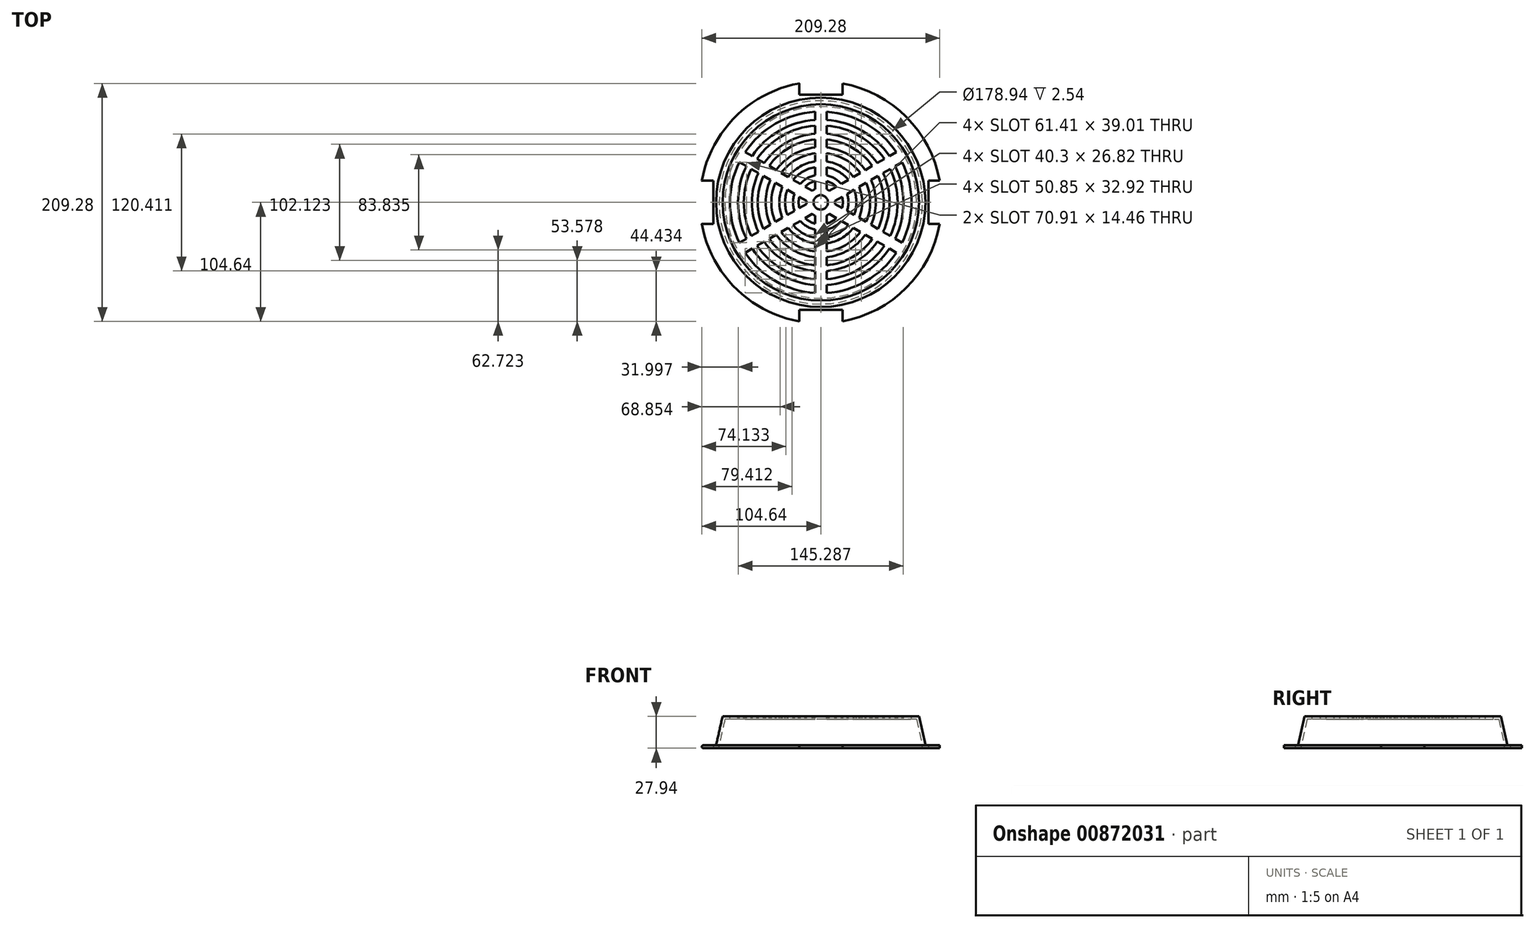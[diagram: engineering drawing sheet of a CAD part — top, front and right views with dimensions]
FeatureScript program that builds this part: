
annotation { "Feature Type Name" : "Feature", "Feature Type Description" : "" }
export const myFeature = defineFeature(function(context is Context, id is Id, definition is map)
    precondition{}
    {
        {
            var Q0;
            Q0=qCreatedBy(makeId("Front.planeOp"),FACE);
            var sketch = newSketch(context, id + "F0", { "sketchPlane" : qUnion([Q0])});
            skLineSegment(sketch, "E0", {"start": v(0, 0) * mm, "end": v(0, 69.45) * mm, "construction": true});
            skLineSegment(sketch, "E1", {"start": v(0, 0) * mm, "end": v(-92.08, 0) * mm});
            skLineSegment(sketch, "E2", {"start": v(-92.08, 0) * mm, "end": v(-86.36, 25.4) * mm});
            skLineSegment(sketch, "E3", {"start": v(-86.36, 25.4) * mm, "end": v(0, 25.4) * mm});
            skLineSegment(sketch, "E4", {"start": v(0, 25.4) * mm, "end": v(0, 0) * mm});
            skSolve(sketch);
        }
        {
            var Q0;
            Q0=makeQuery(id+"F0.imprint","IMPRINT",FACE,{"disambiguationData":[TD([[makeQuery(id+"F0.imprint","IMPRINT",EDGE,{"derivedFrom":sQuery(id+"F0.wireOp",EDGE,"E1")}),-1.0]])]});
            var Q1;
            Q1=sQuery(id+"F0.wireOp",EDGE,"E0");
            revolve(context, id + "F1", {"surfaceOperationType" : NewSurfaceOperationType.NEW, "entities" : qUnion([Q0]), "axis" : qUnion([Q1]), "revolveType" : RevolveType.FULL});
        }
        {
            var Q0;
            Q0=makeQuery(id+"F1.opRevolve","SWEPT_FACE",FACE,{"disambiguationData":[OSD([sQuery(id+"F0.wireOp",EDGE,"E1")])]});
            shell(context, id + "F2", {"entities" : qUnion([Q0]), "thickness" : 2.54 * mm});
        }
        {
            var Q0;
            Q0=makeQuery(id+"F1.opRevolve","SWEPT_FACE",FACE,{"disambiguationData":[OSD([sQuery(id+"F0.wireOp",EDGE,"E1")])]});
            var sketch = newSketch(context, id + "F3", { "sketchPlane" : qUnion([Q0])});
            skCircle(sketch, "E5.0", {"center": v(0, 0) * mm, "radius": 89.47 * mm});
            skCircle(sketch, "E6", {"center": v(0, 0) * mm, "radius": 106.36 * mm});
            skSolve(sketch);
        }
        {
            var Q0;
            Q0 = qSketchRegion(id + "F3", true);
            extrude(context, id + "F4", {"entities" : qUnion([Q0]), "operationType" : NewBodyOperationType.ADD, "depth" : 2.54 * mm, "offsetDistance" : 25.4 * mm});
        }
        {
            var Q0;
            Q0=makeQuery(id+"F1.opRevolve","SWEPT_FACE",FACE,{"disambiguationData":[OSD([sQuery(id+"F0.wireOp",EDGE,"E3")])]});
            var sketch = newSketch(context, id + "F5", { "sketchPlane" : qUnion([Q0])});
            skLineSegment(sketch, "E7", {"start": v(0, 0) * mm, "end": v(0, 86.36) * mm, "construction": true});
            skLineSegment(sketch, "E8", {"start": v(0, 0) * mm, "end": v(74.79, 43.18) * mm, "construction": true});
            skArc(sketch, "E9", {"start": v(5.08, 23.83) * mm, "mid": v(12.18, 21.1) * mm, "end": v(18.1, 16.32) * mm});
            skArc(sketch, "E10", {"start": v(5.08, 18.75) * mm, "mid": v(9.71, 16.82) * mm, "end": v(13.7, 13.78) * mm});
            skArc(sketch, "E11", {"start": v(5.08, 30.94) * mm, "mid": v(15.68, 27.16) * mm, "end": v(24.26, 19.87) * mm});
            skArc(sketch, "E12", {"start": v(5.08, 11.64) * mm, "mid": v(6.35, 11) * mm, "end": v(7.54, 10.22) * mm});
            skLineSegment(sketch, "E13", {"start": v(24.26, 19.87) * mm, "end": v(18.1, 16.32) * mm});
            skLineSegment(sketch, "E14", {"start": v(5.08, 23.83) * mm, "end": v(5.08, 30.94) * mm});
            skLineSegment(sketch, "E15", {"start": v(5.08, 18.75) * mm, "end": v(5.08, 11.64) * mm});
            skLineSegment(sketch, "E16", {"start": v(7.54, 10.22) * mm, "end": v(13.7, 13.78) * mm});
            skArc(sketch, "E17", {"start": v(5.08, 36.02) * mm, "mid": v(18.2, 31.5) * mm, "end": v(28.66, 22.41) * mm});
            skArc(sketch, "E18", {"start": v(5.08, 43.14) * mm, "mid": v(21.72, 37.61) * mm, "end": v(34.82, 25.97) * mm});
            skLineSegment(sketch, "E19", {"start": v(5.08, 36.02) * mm, "end": v(5.08, 43.14) * mm});
            skLineSegment(sketch, "E20", {"start": v(28.66, 22.41) * mm, "end": v(34.82, 25.97) * mm});
            skArc(sketch, "E21", {"start": v(5.08, 48.22) * mm, "mid": v(24.24, 41.99) * mm, "end": v(39.22, 28.5) * mm});
            skArc(sketch, "E22", {"start": v(5.08, 55.33) * mm, "mid": v(27.78, 48.12) * mm, "end": v(45.38, 32.06) * mm});
            skLineSegment(sketch, "E23", {"start": v(5.08, 48.22) * mm, "end": v(5.08, 55.33) * mm});
            skLineSegment(sketch, "E24", {"start": v(39.22, 28.5) * mm, "end": v(45.38, 32.06) * mm});
            skArc(sketch, "E25.1.0", {"start": v(-45.38, 32.06) * mm, "mid": v(-27.78, 48.12) * mm, "end": v(-5.08, 55.33) * mm});
            skLineSegment(sketch, "E25.1.1", {"start": v(-5.08, 48.22) * mm, "end": v(-5.08, 55.33) * mm});
            skArc(sketch, "E25.1.2", {"start": v(-39.22, 28.5) * mm, "mid": v(-24.24, 41.99) * mm, "end": v(-5.08, 48.22) * mm});
            skLineSegment(sketch, "E25.1.3", {"start": v(-39.22, 28.5) * mm, "end": v(-45.38, 32.06) * mm});
            skLineSegment(sketch, "E25.1.4", {"start": v(-28.66, 22.41) * mm, "end": v(-34.82, 25.97) * mm});
            skArc(sketch, "E25.1.5", {"start": v(-34.82, 25.97) * mm, "mid": v(-21.72, 37.61) * mm, "end": v(-5.08, 43.14) * mm});
            skLineSegment(sketch, "E25.1.6", {"start": v(-5.08, 36.02) * mm, "end": v(-5.08, 43.14) * mm});
            skArc(sketch, "E25.1.7", {"start": v(-28.66, 22.41) * mm, "mid": v(-18.2, 31.5) * mm, "end": v(-5.08, 36.02) * mm});
            skArc(sketch, "E25.1.8", {"start": v(-24.26, 19.87) * mm, "mid": v(-15.68, 27.16) * mm, "end": v(-5.08, 30.94) * mm});
            skLineSegment(sketch, "E25.1.9", {"start": v(-18.1, 16.32) * mm, "end": v(-24.26, 19.87) * mm});
            skArc(sketch, "E25.1.10", {"start": v(-18.1, 16.32) * mm, "mid": v(-12.18, 21.1) * mm, "end": v(-5.08, 23.83) * mm});
            skLineSegment(sketch, "E25.1.11", {"start": v(-5.08, 30.94) * mm, "end": v(-5.08, 23.83) * mm});
            skArc(sketch, "E25.1.12", {"start": v(-13.7, 13.78) * mm, "mid": v(-9.71, 16.82) * mm, "end": v(-5.08, 18.75) * mm});
            skLineSegment(sketch, "E25.1.13", {"start": v(-13.7, 13.78) * mm, "end": v(-7.54, 10.22) * mm});
            skArc(sketch, "E25.1.14", {"start": v(-7.54, 10.22) * mm, "mid": v(-6.35, 11) * mm, "end": v(-5.08, 11.64) * mm});
            skLineSegment(sketch, "E25.1.15", {"start": v(-5.08, 11.64) * mm, "end": v(-5.08, 18.75) * mm});
            skArc(sketch, "E25.2.0", {"start": v(-50.46, -23.26) * mm, "mid": v(-55.56, 0) * mm, "end": v(-50.46, 23.26) * mm});
            skLineSegment(sketch, "E25.2.1", {"start": v(-44.3, 19.7) * mm, "end": v(-50.46, 23.26) * mm});
            skArc(sketch, "E25.2.2", {"start": v(-44.3, -19.7) * mm, "mid": v(-48.48, 0) * mm, "end": v(-44.3, 19.7) * mm});
            skLineSegment(sketch, "E25.2.3", {"start": v(-44.3, -19.7) * mm, "end": v(-50.46, -23.26) * mm});
            skLineSegment(sketch, "E25.2.4", {"start": v(-33.74, -13.61) * mm, "end": v(-39.9, -17.17) * mm});
            skArc(sketch, "E25.2.5", {"start": v(-39.9, -17.17) * mm, "mid": v(-43.43, 0) * mm, "end": v(-39.9, 17.17) * mm});
            skLineSegment(sketch, "E25.2.6", {"start": v(-33.74, 13.61) * mm, "end": v(-39.9, 17.17) * mm});
            skArc(sketch, "E25.2.7", {"start": v(-33.74, -13.61) * mm, "mid": v(-36.38, 0) * mm, "end": v(-33.74, 13.61) * mm});
            skArc(sketch, "E25.2.8", {"start": v(-29.34, -11.07) * mm, "mid": v(-31.36, 0) * mm, "end": v(-29.34, 11.07) * mm});
            skLineSegment(sketch, "E25.2.9", {"start": v(-23.18, -7.52) * mm, "end": v(-29.34, -11.07) * mm});
            skArc(sketch, "E25.2.10", {"start": v(-23.18, -7.52) * mm, "mid": v(-24.37, 0) * mm, "end": v(-23.18, 7.52) * mm});
            skLineSegment(sketch, "E25.2.11", {"start": v(-29.34, 11.07) * mm, "end": v(-23.18, 7.52) * mm});
            skArc(sketch, "E25.2.12", {"start": v(-18.78, -4.98) * mm, "mid": v(-19.43, 0) * mm, "end": v(-18.78, 4.98) * mm});
            skLineSegment(sketch, "E25.2.13", {"start": v(-18.78, -4.98) * mm, "end": v(-12.62, -1.42) * mm});
            skArc(sketch, "E25.2.14", {"start": v(-12.62, -1.42) * mm, "mid": v(-12.7, 0) * mm, "end": v(-12.62, 1.42) * mm});
            skLineSegment(sketch, "E25.2.15", {"start": v(-12.62, 1.42) * mm, "end": v(-18.78, 4.98) * mm});
            skArc(sketch, "E25.3.0", {"start": v(-5.08, -55.33) * mm, "mid": v(-27.78, -48.12) * mm, "end": v(-45.38, -32.06) * mm});
            skLineSegment(sketch, "E25.3.1", {"start": v(-39.22, -28.5) * mm, "end": v(-45.38, -32.06) * mm});
            skArc(sketch, "E25.3.2", {"start": v(-5.08, -48.22) * mm, "mid": v(-24.24, -41.99) * mm, "end": v(-39.22, -28.5) * mm});
            skLineSegment(sketch, "E25.3.3", {"start": v(-5.08, -48.22) * mm, "end": v(-5.08, -55.33) * mm});
            skLineSegment(sketch, "E25.3.4", {"start": v(-5.08, -36.02) * mm, "end": v(-5.08, -43.14) * mm});
            skArc(sketch, "E25.3.5", {"start": v(-5.08, -43.14) * mm, "mid": v(-21.72, -37.61) * mm, "end": v(-34.82, -25.97) * mm});
            skLineSegment(sketch, "E25.3.6", {"start": v(-28.66, -22.41) * mm, "end": v(-34.82, -25.97) * mm});
            skArc(sketch, "E25.3.7", {"start": v(-5.08, -36.02) * mm, "mid": v(-18.2, -31.5) * mm, "end": v(-28.66, -22.41) * mm});
            skArc(sketch, "E25.3.8", {"start": v(-5.08, -30.94) * mm, "mid": v(-15.68, -27.16) * mm, "end": v(-24.26, -19.87) * mm});
            skLineSegment(sketch, "E25.3.9", {"start": v(-5.08, -23.83) * mm, "end": v(-5.08, -30.94) * mm});
            skArc(sketch, "E25.3.10", {"start": v(-5.08, -23.83) * mm, "mid": v(-12.18, -21.1) * mm, "end": v(-18.1, -16.32) * mm});
            skLineSegment(sketch, "E25.3.11", {"start": v(-24.26, -19.87) * mm, "end": v(-18.1, -16.32) * mm});
            skArc(sketch, "E25.3.12", {"start": v(-5.08, -18.75) * mm, "mid": v(-9.71, -16.82) * mm, "end": v(-13.7, -13.78) * mm});
            skLineSegment(sketch, "E25.3.13", {"start": v(-5.08, -18.75) * mm, "end": v(-5.08, -11.64) * mm});
            skArc(sketch, "E25.3.14", {"start": v(-5.08, -11.64) * mm, "mid": v(-6.35, -11) * mm, "end": v(-7.54, -10.22) * mm});
            skLineSegment(sketch, "E25.3.15", {"start": v(-7.54, -10.22) * mm, "end": v(-13.7, -13.78) * mm});
            skArc(sketch, "E25.4.0", {"start": v(45.38, -32.06) * mm, "mid": v(27.78, -48.12) * mm, "end": v(5.08, -55.33) * mm});
            skLineSegment(sketch, "E25.4.1", {"start": v(5.08, -48.22) * mm, "end": v(5.08, -55.33) * mm});
            skArc(sketch, "E25.4.2", {"start": v(39.22, -28.5) * mm, "mid": v(24.24, -41.99) * mm, "end": v(5.08, -48.22) * mm});
            skLineSegment(sketch, "E25.4.3", {"start": v(39.22, -28.5) * mm, "end": v(45.38, -32.06) * mm});
            skLineSegment(sketch, "E25.4.4", {"start": v(28.66, -22.41) * mm, "end": v(34.82, -25.97) * mm});
            skArc(sketch, "E25.4.5", {"start": v(34.82, -25.97) * mm, "mid": v(21.72, -37.61) * mm, "end": v(5.08, -43.14) * mm});
            skLineSegment(sketch, "E25.4.6", {"start": v(5.08, -36.02) * mm, "end": v(5.08, -43.14) * mm});
            skArc(sketch, "E25.4.7", {"start": v(28.66, -22.41) * mm, "mid": v(18.2, -31.5) * mm, "end": v(5.08, -36.02) * mm});
            skArc(sketch, "E25.4.8", {"start": v(24.26, -19.87) * mm, "mid": v(15.68, -27.16) * mm, "end": v(5.08, -30.94) * mm});
            skLineSegment(sketch, "E25.4.9", {"start": v(18.1, -16.32) * mm, "end": v(24.26, -19.87) * mm});
            skArc(sketch, "E25.4.10", {"start": v(18.1, -16.32) * mm, "mid": v(12.18, -21.1) * mm, "end": v(5.08, -23.83) * mm});
            skLineSegment(sketch, "E25.4.11", {"start": v(5.08, -30.94) * mm, "end": v(5.08, -23.83) * mm});
            skArc(sketch, "E25.4.12", {"start": v(13.7, -13.78) * mm, "mid": v(9.71, -16.82) * mm, "end": v(5.08, -18.75) * mm});
            skLineSegment(sketch, "E25.4.13", {"start": v(13.7, -13.78) * mm, "end": v(7.54, -10.22) * mm});
            skArc(sketch, "E25.4.14", {"start": v(7.54, -10.22) * mm, "mid": v(6.35, -11) * mm, "end": v(5.08, -11.64) * mm});
            skLineSegment(sketch, "E25.4.15", {"start": v(5.08, -11.64) * mm, "end": v(5.08, -18.75) * mm});
            skArc(sketch, "E25.5.0", {"start": v(50.46, 23.26) * mm, "mid": v(55.56, 0) * mm, "end": v(50.46, -23.26) * mm});
            skLineSegment(sketch, "E25.5.1", {"start": v(44.3, -19.7) * mm, "end": v(50.46, -23.26) * mm});
            skArc(sketch, "E25.5.2", {"start": v(44.3, 19.7) * mm, "mid": v(48.48, 0) * mm, "end": v(44.3, -19.7) * mm});
            skLineSegment(sketch, "E25.5.3", {"start": v(44.3, 19.7) * mm, "end": v(50.46, 23.26) * mm});
            skLineSegment(sketch, "E25.5.4", {"start": v(33.74, 13.61) * mm, "end": v(39.9, 17.17) * mm});
            skArc(sketch, "E25.5.5", {"start": v(39.9, 17.17) * mm, "mid": v(43.43, 0) * mm, "end": v(39.9, -17.17) * mm});
            skLineSegment(sketch, "E25.5.6", {"start": v(33.74, -13.61) * mm, "end": v(39.9, -17.17) * mm});
            skArc(sketch, "E25.5.7", {"start": v(33.74, 13.61) * mm, "mid": v(36.38, 0) * mm, "end": v(33.74, -13.61) * mm});
            skArc(sketch, "E25.5.8", {"start": v(29.34, 11.07) * mm, "mid": v(31.36, 0) * mm, "end": v(29.34, -11.07) * mm});
            skLineSegment(sketch, "E25.5.9", {"start": v(23.18, 7.52) * mm, "end": v(29.34, 11.07) * mm});
            skArc(sketch, "E25.5.10", {"start": v(23.18, 7.52) * mm, "mid": v(24.37, 0) * mm, "end": v(23.18, -7.52) * mm});
            skLineSegment(sketch, "E25.5.11", {"start": v(29.34, -11.07) * mm, "end": v(23.18, -7.52) * mm});
            skArc(sketch, "E25.5.12", {"start": v(18.78, 4.98) * mm, "mid": v(19.43, 0) * mm, "end": v(18.78, -4.98) * mm});
            skLineSegment(sketch, "E25.5.13", {"start": v(18.78, 4.98) * mm, "end": v(12.62, 1.42) * mm});
            skArc(sketch, "E25.5.14", {"start": v(12.62, 1.42) * mm, "mid": v(12.7, 0) * mm, "end": v(12.62, -1.42) * mm});
            skLineSegment(sketch, "E25.5.15", {"start": v(12.62, -1.42) * mm, "end": v(18.78, -4.98) * mm});
            skArc(sketch, "E26", {"start": v(5.08, 60.4) * mm, "mid": v(30.31, 52.5) * mm, "end": v(49.77, 34.6) * mm});
            skArc(sketch, "E27", {"start": v(5.08, 67.52) * mm, "mid": v(33.86, 58.64) * mm, "end": v(55.93, 38.16) * mm});
            skPoint(sketch, "E27.startSnap0", {"position": v(5.08, 39.58) * mm});
            skLineSegment(sketch, "E28", {"start": v(5.08, 60.4) * mm, "end": v(5.08, 67.52) * mm});
            skLineSegment(sketch, "E29", {"start": v(49.77, 34.6) * mm, "end": v(55.93, 38.16) * mm});
            skArc(sketch, "E30", {"start": v(5.08, 72.6) * mm, "mid": v(36.39, 63.03) * mm, "end": v(60.33, 40.7) * mm});
            skArc(sketch, "E31", {"start": v(5.08, 79.71) * mm, "mid": v(39.94, 69.17) * mm, "end": v(66.5, 44.26) * mm});
            skLineSegment(sketch, "E32", {"start": v(5.08, 72.6) * mm, "end": v(5.08, 79.71) * mm});
            skLineSegment(sketch, "E33", {"start": v(60.33, 40.7) * mm, "end": v(66.5, 44.26) * mm});
            skArc(sketch, "E34.1.0", {"start": v(-49.77, 34.6) * mm, "mid": v(-30.31, 52.5) * mm, "end": v(-5.08, 60.4) * mm});
            skLineSegment(sketch, "E34.1.1", {"start": v(-49.77, 34.6) * mm, "end": v(-55.93, 38.16) * mm});
            skArc(sketch, "E34.1.2", {"start": v(-55.93, 38.16) * mm, "mid": v(-33.86, 58.64) * mm, "end": v(-5.08, 67.52) * mm});
            skLineSegment(sketch, "E34.1.3", {"start": v(-5.08, 60.4) * mm, "end": v(-5.08, 67.52) * mm});
            skLineSegment(sketch, "E34.1.4", {"start": v(-5.08, 72.6) * mm, "end": v(-5.08, 79.71) * mm});
            skArc(sketch, "E34.1.5", {"start": v(-60.33, 40.7) * mm, "mid": v(-36.39, 63.03) * mm, "end": v(-5.08, 72.6) * mm});
            skLineSegment(sketch, "E34.1.6", {"start": v(-60.33, 40.7) * mm, "end": v(-66.5, 44.26) * mm});
            skArc(sketch, "E34.1.7", {"start": v(-66.5, 44.26) * mm, "mid": v(-39.94, 69.17) * mm, "end": v(-5.08, 79.71) * mm});
            skArc(sketch, "E34.2.0", {"start": v(-54.85, -25.8) * mm, "mid": v(-60.62, 0) * mm, "end": v(-54.85, 25.8) * mm});
            skLineSegment(sketch, "E34.2.1", {"start": v(-54.85, -25.8) * mm, "end": v(-61.01, -29.36) * mm});
            skArc(sketch, "E34.2.2", {"start": v(-61.01, -29.36) * mm, "mid": v(-67.71, 0) * mm, "end": v(-61.01, 29.36) * mm});
            skLineSegment(sketch, "E34.2.3", {"start": v(-54.85, 25.8) * mm, "end": v(-61.01, 29.36) * mm});
            skLineSegment(sketch, "E34.2.4", {"start": v(-65.41, 31.9) * mm, "end": v(-71.57, 35.46) * mm});
            skArc(sketch, "E34.2.5", {"start": v(-65.41, -31.9) * mm, "mid": v(-72.78, 0) * mm, "end": v(-65.41, 31.9) * mm});
            skLineSegment(sketch, "E34.2.6", {"start": v(-65.41, -31.9) * mm, "end": v(-71.57, -35.46) * mm});
            skArc(sketch, "E34.2.7", {"start": v(-71.57, -35.46) * mm, "mid": v(-79.87, 0) * mm, "end": v(-71.57, 35.46) * mm});
            skArc(sketch, "E34.3.0", {"start": v(-5.08, -60.4) * mm, "mid": v(-30.31, -52.5) * mm, "end": v(-49.77, -34.6) * mm});
            skLineSegment(sketch, "E34.3.1", {"start": v(-5.08, -60.4) * mm, "end": v(-5.08, -67.52) * mm});
            skArc(sketch, "E34.3.2", {"start": v(-5.08, -67.52) * mm, "mid": v(-33.86, -58.64) * mm, "end": v(-55.93, -38.16) * mm});
            skLineSegment(sketch, "E34.3.3", {"start": v(-49.77, -34.6) * mm, "end": v(-55.93, -38.16) * mm});
            skLineSegment(sketch, "E34.3.4", {"start": v(-60.33, -40.7) * mm, "end": v(-66.5, -44.26) * mm});
            skArc(sketch, "E34.3.5", {"start": v(-5.08, -72.6) * mm, "mid": v(-36.39, -63.03) * mm, "end": v(-60.33, -40.7) * mm});
            skLineSegment(sketch, "E34.3.6", {"start": v(-5.08, -72.6) * mm, "end": v(-5.08, -79.71) * mm});
            skArc(sketch, "E34.3.7", {"start": v(-5.08, -79.71) * mm, "mid": v(-39.94, -69.17) * mm, "end": v(-66.5, -44.26) * mm});
            skArc(sketch, "E34.4.0", {"start": v(49.77, -34.6) * mm, "mid": v(30.31, -52.5) * mm, "end": v(5.08, -60.4) * mm});
            skLineSegment(sketch, "E34.4.1", {"start": v(49.77, -34.6) * mm, "end": v(55.93, -38.16) * mm});
            skArc(sketch, "E34.4.2", {"start": v(55.93, -38.16) * mm, "mid": v(33.86, -58.64) * mm, "end": v(5.08, -67.52) * mm});
            skLineSegment(sketch, "E34.4.3", {"start": v(5.08, -60.4) * mm, "end": v(5.08, -67.52) * mm});
            skLineSegment(sketch, "E34.4.4", {"start": v(5.08, -72.6) * mm, "end": v(5.08, -79.71) * mm});
            skArc(sketch, "E34.4.5", {"start": v(60.33, -40.7) * mm, "mid": v(36.39, -63.03) * mm, "end": v(5.08, -72.6) * mm});
            skLineSegment(sketch, "E34.4.6", {"start": v(60.33, -40.7) * mm, "end": v(66.5, -44.26) * mm});
            skArc(sketch, "E34.4.7", {"start": v(66.5, -44.26) * mm, "mid": v(39.94, -69.17) * mm, "end": v(5.08, -79.71) * mm});
            skArc(sketch, "E34.5.0", {"start": v(54.85, 25.8) * mm, "mid": v(60.62, 0) * mm, "end": v(54.85, -25.8) * mm});
            skLineSegment(sketch, "E34.5.1", {"start": v(54.85, 25.8) * mm, "end": v(61.01, 29.36) * mm});
            skArc(sketch, "E34.5.2", {"start": v(61.01, 29.36) * mm, "mid": v(67.71, 0) * mm, "end": v(61.01, -29.36) * mm});
            skLineSegment(sketch, "E34.5.3", {"start": v(54.85, -25.8) * mm, "end": v(61.01, -29.36) * mm});
            skLineSegment(sketch, "E34.5.4", {"start": v(65.41, -31.9) * mm, "end": v(71.57, -35.46) * mm});
            skArc(sketch, "E34.5.5", {"start": v(65.41, 31.9) * mm, "mid": v(72.78, 0) * mm, "end": v(65.41, -31.9) * mm});
            skLineSegment(sketch, "E34.5.6", {"start": v(65.41, 31.9) * mm, "end": v(71.57, 35.46) * mm});
            skArc(sketch, "E34.5.7", {"start": v(71.57, 35.46) * mm, "mid": v(79.87, 0) * mm, "end": v(71.57, -35.46) * mm});
            skSolve(sketch);
        }
        {
            var Q0;
            Q0 = qSketchRegion(id + "F5", true);
            extrude(context, id + "F6", {"entities" : qUnion([Q0]), "operationType" : NewBodyOperationType.REMOVE, "endBound" : BoundingType.THROUGH_ALL, "oppositeDirection" : true, "depth" : 25.4 * mm, "offsetDistance" : 25.4 * mm});
        }
        {
            var Q0;
            Q0=makeQuery(id+"F4.opExtrude","CAP_FACE",FACE,{"disambiguationData":[OSD([sQuery(id+"F3.wireOp",EDGE,"E5.0"),sQuery(id+"F3.wireOp",EDGE,"E6")])],"isStart":false});
            var sketch = newSketch(context, id + "F7", { "sketchPlane" : qUnion([Q0])});
            skLineSegment(sketch, "E35", {"start": v(-28.47, 0) * mm, "end": v(28.47, 0) * mm, "construction": true});
            skLineSegment(sketch, "E36.bottom", {"start": v(-119.87, 19.05) * mm, "end": v(-94.62, 19.05) * mm});
            skLineSegment(sketch, "E36.top", {"start": v(-119.87, -19.05) * mm, "end": v(-94.62, -19.05) * mm});
            skLineSegment(sketch, "E36.left", {"start": v(-119.87, 19.05) * mm, "end": v(-119.87, -19.05) * mm});
            skLineSegment(sketch, "E36.right", {"start": v(-94.62, 19.05) * mm, "end": v(-94.62, -19.05) * mm});
            skLineSegment(sketch, "E37", {"start": v(-94.61, 19.05) * mm, "end": v(-119.87, -19.05) * mm, "construction": true});
            skPoint(sketch, "E38", {"position": v(-107.24, 0) * mm});
            skLineSegment(sketch, "E39", {"start": v(0, 0) * mm, "end": v(0, 52.1) * mm, "construction": true});
            skPoint(sketch, "E39.endSnap0", {"position": v(0, 0) * mm});
            skPoint(sketch, "E40.MirrorP", {"position": v(107.24, 0) * mm});
            skLineSegment(sketch, "E41.MirrorCS", {"start": v(119.87, 19.05) * mm, "end": v(94.62, 19.05) * mm});
            skLineSegment(sketch, "E42.MirrorCS", {"start": v(119.87, -19.05) * mm, "end": v(94.62, -19.05) * mm});
            skLineSegment(sketch, "E43.MirrorCS", {"start": v(119.87, 19.05) * mm, "end": v(119.87, -19.05) * mm});
            skLineSegment(sketch, "E44.MirrorCS", {"start": v(94.62, 19.05) * mm, "end": v(94.62, -19.05) * mm});
            skLineSegment(sketch, "E45.MirrorCS", {"start": v(94.61, 19.05) * mm, "end": v(119.87, -19.05) * mm, "construction": true});
            skLineSegment(sketch, "E46.1.1", {"start": v(19.05, -119.87) * mm, "end": v(19.05, -94.62) * mm});
            skLineSegment(sketch, "E46.1.2", {"start": v(-19.05, -119.87) * mm, "end": v(19.05, -119.87) * mm});
            skLineSegment(sketch, "E46.1.3", {"start": v(-19.05, -119.87) * mm, "end": v(-19.05, -94.62) * mm});
            skLineSegment(sketch, "E46.1.4", {"start": v(-19.05, -94.62) * mm, "end": v(19.05, -94.62) * mm});
            skLineSegment(sketch, "E46.1.5", {"start": v(-19.05, -94.61) * mm, "end": v(19.05, -119.87) * mm, "construction": true});
            skLineSegment(sketch, "E46.2.2", {"start": v(119.87, -19.05) * mm, "end": v(119.87, 19.05) * mm});
            skLineSegment(sketch, "E46.2.4", {"start": v(94.62, -19.05) * mm, "end": v(94.62, 19.05) * mm});
            skLineSegment(sketch, "E46.2.5", {"start": v(94.61, -19.05) * mm, "end": v(119.87, 19.05) * mm, "construction": true});
            skLineSegment(sketch, "E46.3.1", {"start": v(-19.05, 119.87) * mm, "end": v(-19.05, 94.62) * mm});
            skLineSegment(sketch, "E46.3.2", {"start": v(19.05, 119.87) * mm, "end": v(-19.05, 119.87) * mm});
            skLineSegment(sketch, "E46.3.3", {"start": v(19.05, 119.87) * mm, "end": v(19.05, 94.62) * mm});
            skLineSegment(sketch, "E46.3.4", {"start": v(19.05, 94.62) * mm, "end": v(-19.05, 94.62) * mm});
            skLineSegment(sketch, "E46.3.5", {"start": v(19.05, 94.61) * mm, "end": v(-19.05, 119.87) * mm, "construction": true});
            skSolve(sketch);
        }
        {
            var Q0;
            Q0 = qSketchRegion(id + "F7", true);
            extrude(context, id + "F8", {"entities" : qUnion([Q0]), "operationType" : NewBodyOperationType.REMOVE, "endBound" : BoundingType.THROUGH_ALL, "oppositeDirection" : true, "depth" : 25.4 * mm, "offsetDistance" : 25.4 * mm});
        }
        {
            var Q0;
            Q0=makeQuery(id+"F1.opRevolve","SWEPT_FACE",FACE,{"disambiguationData":[OSD([sQuery(id+"F0.wireOp",EDGE,"E3")])]});
            var sketch = newSketch(context, id + "F9", { "sketchPlane" : qUnion([Q0])});
            skCircle(sketch, "E47", {"center": v(0, 0) * mm, "radius": 6.35 * mm});
            skSolve(sketch);
        }
        {
            var Q0;
            Q0 = qSketchRegion(id + "F9", true);
            extrude(context, id + "F10", {"entities" : qUnion([Q0]), "operationType" : NewBodyOperationType.REMOVE, "endBound" : BoundingType.THROUGH_ALL, "oppositeDirection" : true, "depth" : 25.4 * mm, "offsetDistance" : 25.4 * mm});
        }
        {
            var Q0;
            {var subQ0=sQuery(id+"F3.wireOp",EDGE,"E6");Q0=makeQuery(id+"F8.boolean.opBoolean","SPLIT",EDGE,{"disambiguationData":[TD([makeQuery(id+"F8.opExtrude","SWEPT_FACE",FACE,{"disambiguationData":[OSD([sQuery(id+"F7.wireOp",EDGE,"E36.top")])]})])],"derivedFrom":makeQuery(id+"F4.opExtrude","CAP_EDGE",EDGE,{"disambiguationData":[OSD([subQ0])],"isStart":false})});}
            var Q1;
            {var subQ0=sQuery(id+"F3.wireOp",EDGE,"E6");Q1=makeQuery(id+"F8.boolean.opBoolean","SPLIT",EDGE,{"disambiguationData":[TD([makeQuery(id+"F8.opExtrude","SWEPT_FACE",FACE,{"disambiguationData":[OSD([sQuery(id+"F7.wireOp",EDGE,"E36.top")])]})])],"derivedFrom":makeQuery(id+"F4.opExtrude","CAP_EDGE",EDGE,{"disambiguationData":[OSD([subQ0])],"isStart":true})});}
            var Q2;
            {var subQ0=sQuery(id+"F3.wireOp",EDGE,"E6");Q2=makeQuery(id+"F8.boolean.opBoolean","SPLIT",EDGE,{"disambiguationData":[TD([makeQuery(id+"F8.opExtrude","SWEPT_FACE",FACE,{"disambiguationData":[OSD([sQuery(id+"F7.wireOp",EDGE,"E36.bottom")])]})])],"derivedFrom":makeQuery(id+"F4.opExtrude","CAP_EDGE",EDGE,{"disambiguationData":[OSD([subQ0])],"isStart":true})});}
            var Q3;
            {var subQ0=sQuery(id+"F3.wireOp",EDGE,"E6");Q3=makeQuery(id+"F8.boolean.opBoolean","SPLIT",EDGE,{"disambiguationData":[TD([makeQuery(id+"F8.opExtrude","SWEPT_FACE",FACE,{"disambiguationData":[OSD([sQuery(id+"F7.wireOp",EDGE,"E36.bottom")])]})])],"derivedFrom":makeQuery(id+"F4.opExtrude","CAP_EDGE",EDGE,{"disambiguationData":[OSD([subQ0])],"isStart":false})});}
            fillet(context, id + "F11", {"entities" : qUnion([Q0, Q1, Q2, Q3]), "radius" : 1.27 * mm, "tangentPropagation" : true, "allowEdgeOverflow" : false});
        }
    });
